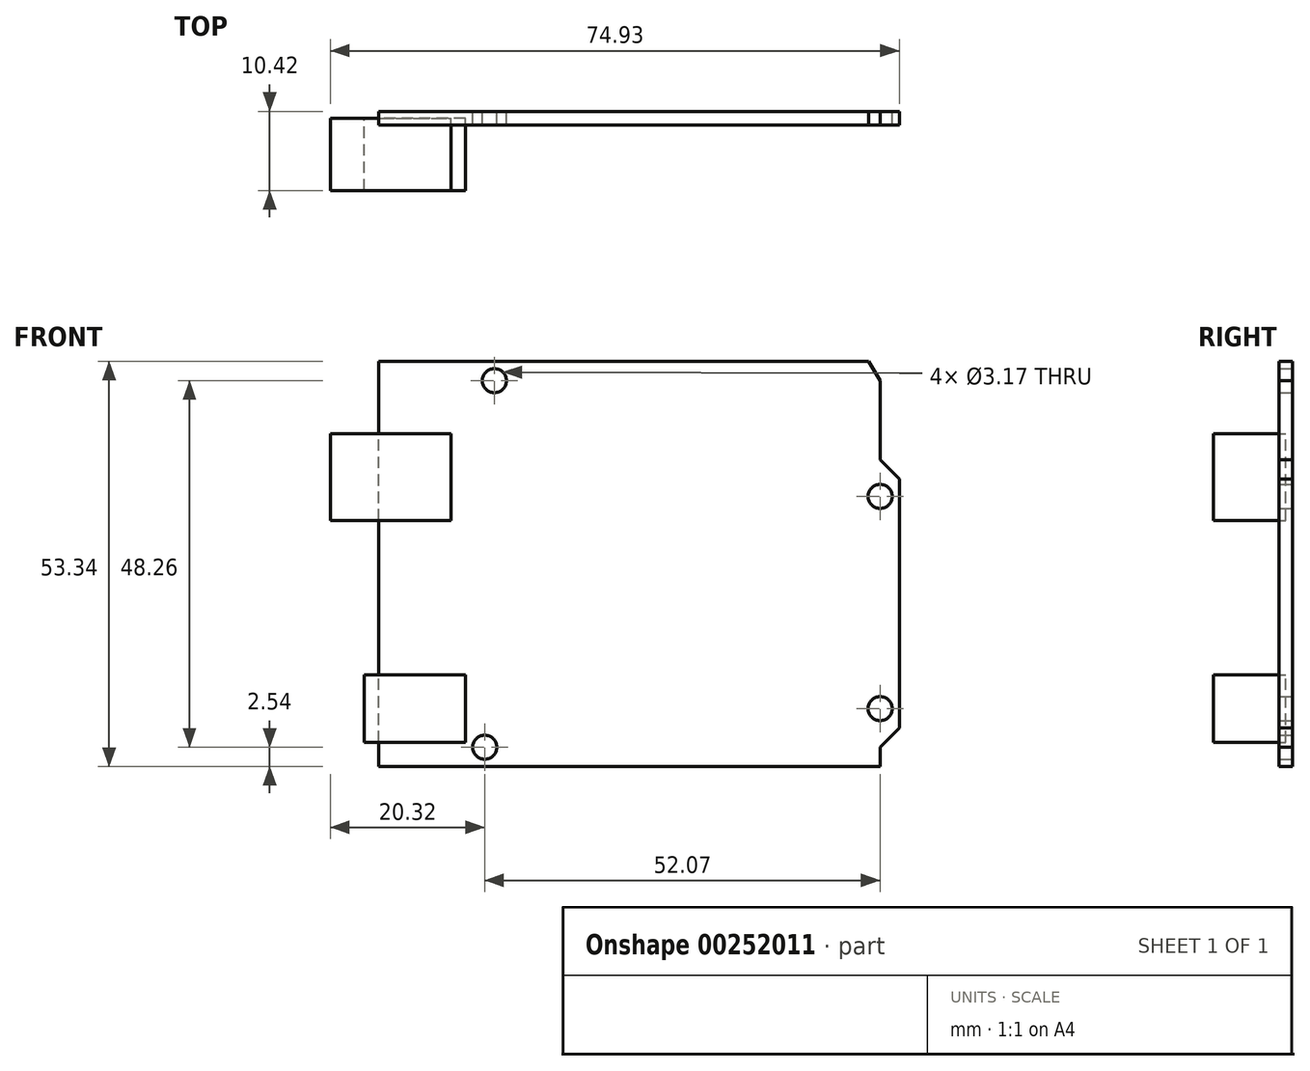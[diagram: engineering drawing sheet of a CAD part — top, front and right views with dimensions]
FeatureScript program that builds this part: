
annotation { "Feature Type Name" : "Feature", "Feature Type Description" : "" }
export const myFeature = defineFeature(function(context is Context, id is Id, definition is map)
    precondition{}
    {
        {
            var Q0;
            Q0=qCreatedBy(makeId("Front.planeOp"),FACE);
            var sketch = newSketch(context, id + "F0", { "sketchPlane" : qUnion([Q0])});
            skLineSegment(sketch, "E0", {"start": v(0, 0) * mm, "end": v(0, 53.34) * mm});
            skLineSegment(sketch, "E1", {"start": v(0, 53.34) * mm, "end": v(64.52, 53.34) * mm});
            skLineSegment(sketch, "E2", {"start": v(0, 0) * mm, "end": v(66.04, 0) * mm});
            skLineSegment(sketch, "E3", {"start": v(66.04, 0) * mm, "end": v(66.04, 2.54) * mm});
            skLineSegment(sketch, "E4", {"start": v(66.04, 50.8) * mm, "end": v(64.52, 53.34) * mm});
            skPoint(sketch, "E5.start.orphan", {"position": v(68.58, 0) * mm});
            skLineSegment(sketch, "E6", {"start": v(66.04, 2.54) * mm, "end": v(68.58, 5.08) * mm});
            skPoint(sketch, "E7.end.orphan", {"position": v(68.58, 2.54) * mm});
            skLineSegment(sketch, "E8", {"start": v(68.58, 5.08) * mm, "end": v(68.58, 37.85) * mm});
            skLineSegment(sketch, "E9", {"start": v(66.04, 40.39) * mm, "end": v(68.58, 37.85) * mm});
            skLineSegment(sketch, "E10.trimOffspring", {"start": v(66.04, 40.39) * mm, "end": v(66.04, 50.8) * mm});
            skSolve(sketch);
        }
        {
            var Q0;
            Q0=qCreatedBy(makeId("Front.planeOp"),FACE);
            var sketch = newSketch(context, id + "F1", { "sketchPlane" : qUnion([Q0])});
            skLineSegment(sketch, "E11", {"start": v(0, 0) * mm, "end": v(0, 3.18) * mm});
            skLineSegment(sketch, "E12", {"start": v(0, 3.18) * mm, "end": v(-1.9, 3.18) * mm});
            skLineSegment(sketch, "E13", {"start": v(0, 12.07) * mm, "end": v(-1.9, 12.07) * mm});
            skLineSegment(sketch, "E14", {"start": v(-1.9, 3.17) * mm, "end": v(-1.9, 12.07) * mm});
            skLineSegment(sketch, "E15", {"start": v(0, 3.18) * mm, "end": v(11.43, 3.18) * mm});
            skLineSegment(sketch, "E16", {"start": v(11.43, 3.17) * mm, "end": v(11.43, 12.07) * mm});
            skLineSegment(sketch, "E17", {"start": v(11.43, 12.07) * mm, "end": v(0, 12.07) * mm});
            skLineSegment(sketch, "E18", {"start": v(-6.35, 0) * mm, "end": v(-6.35, 32.39) * mm});
            skLineSegment(sketch, "E19", {"start": v(-6.35, 32.39) * mm, "end": v(-6.35, 43.82) * mm});
            skLineSegment(sketch, "E20", {"start": v(-6.35, 32.39) * mm, "end": v(0, 32.39) * mm});
            skLineSegment(sketch, "E21", {"start": v(0, 32.39) * mm, "end": v(9.53, 32.39) * mm});
            skLineSegment(sketch, "E22", {"start": v(-6.35, 43.82) * mm, "end": v(9.52, 43.82) * mm});
            skLineSegment(sketch, "E23", {"start": v(9.52, 43.82) * mm, "end": v(9.53, 32.39) * mm});
            skPoint(sketch, "E24.start.orphan", {"position": v(0, 49.34) * mm});
            skSolve(sketch);
        }
        {
            var Q0;
            Q0=makeQuery(id+"F0.imprint","IMPRINT",FACE,{"disambiguationData":[TD([[makeQuery(id+"F0.imprint","IMPRINT",EDGE,{"derivedFrom":sQuery(id+"F0.wireOp",EDGE,"E0")}),-1.0]])]});
            var sketch = newSketch(context, id + "F2", { "sketchPlane" : qUnion([Q0])});
            skPoint(sketch, "E25.start.orphan", {"position": v(0, 123.58) * mm});
            skCircle(sketch, "E26", {"center": v(15.24, 50.8) * mm, "radius": 1.59 * mm});
            skPoint(sketch, "E27.orphan", {"position": v(15.24, 0) * mm});
            skPoint(sketch, "E28.orphan", {"position": v(0, 50.8) * mm});
            skCircle(sketch, "E29", {"center": v(13.97, 2.54) * mm, "radius": 1.59 * mm});
            skPoint(sketch, "E30.orphan", {"position": v(13.97, 0) * mm});
            skPoint(sketch, "E31.start.orphan", {"position": v(0, 2.54) * mm});
            skCircle(sketch, "E32", {"center": v(66.04, 7.62) * mm, "radius": 1.59 * mm});
            skPoint(sketch, "E33.orphan", {"position": v(0, 7.62) * mm});
            skPoint(sketch, "E34.orphan", {"position": v(66.04, 0) * mm});
            skLineSegment(sketch, "E35", {"start": v(66.04, 6.03) * mm, "end": v(66.04, 9.2) * mm});
            skCircle(sketch, "E36", {"center": v(66.04, 35.56) * mm, "radius": 1.59 * mm});
            skPoint(sketch, "E37.orphan", {"position": v(0, 35.56) * mm});
            skSolve(sketch);
        }
        {
            var Q0;
            Q0=makeQuery(id+"F0.imprint","IMPRINT",FACE,{"disambiguationData":[TD([[makeQuery(id+"F0.imprint","IMPRINT",EDGE,{"derivedFrom":sQuery(id+"F0.wireOp",EDGE,"E0")}),-1.0]])]});
            extrude(context, id + "F3", {"entities" : qUnion([Q0]), "endBound" : BoundingType.SYMMETRIC, "depth" : 1.78 * mm});
        }
        {
            var Q0;
            Q0 = qSketchRegion(id + "F1", true);
            extrude(context, id + "F4", {"entities" : qUnion([Q0]), "depth" : 9.52 * mm});
        }
        {
            var Q0;
            Q0 = qSketchRegion(id + "F2", true);
            extrude(context, id + "F5", {"entities" : qUnion([Q0]), "operationType" : NewBodyOperationType.REMOVE, "endBound" : BoundingType.SYMMETRIC, "depth" : 25.4 * mm});
        }
    });
